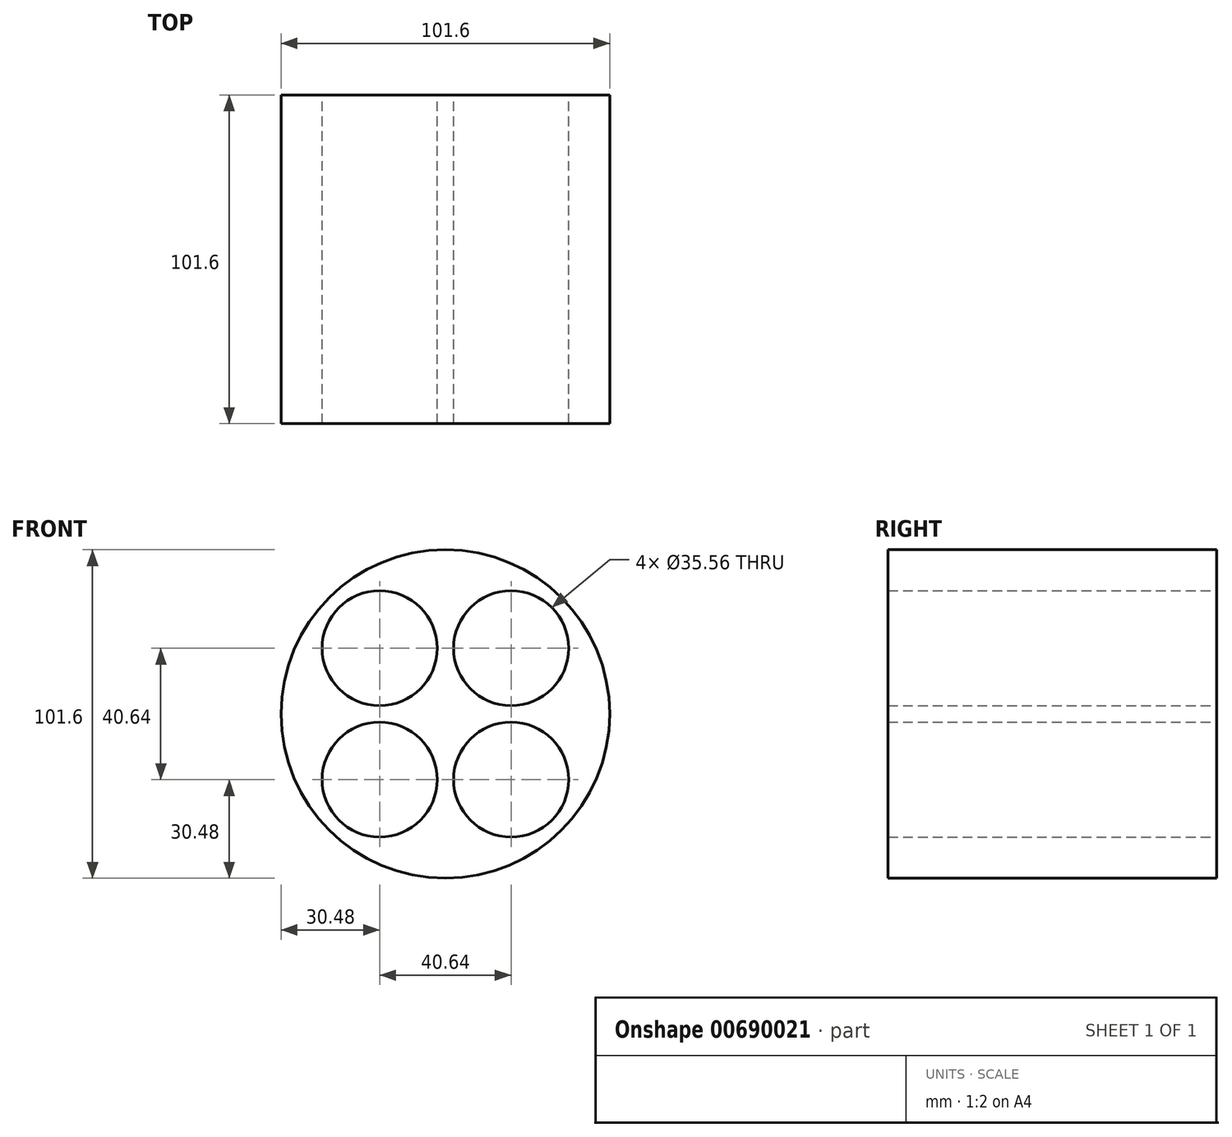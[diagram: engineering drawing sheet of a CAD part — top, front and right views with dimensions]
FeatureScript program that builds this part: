
annotation { "Feature Type Name" : "Feature", "Feature Type Description" : "" }
export const myFeature = defineFeature(function(context is Context, id is Id, definition is map)
    precondition{}
    {
        {
            var Q0;
            Q0=qCreatedBy(makeId("Front.planeOp"),FACE);
            var sketch = newSketch(context, id + "F0", { "sketchPlane" : qUnion([Q0])});
            skCircle(sketch, "E0", {"center": v(0, 0) * mm, "radius": 50.8 * mm});
            skLineSegment(sketch, "E1.bottom", {"start": v(20.32, 20.32) * mm, "end": v(-20.32, 20.32) * mm, "construction": true});
            skLineSegment(sketch, "E1.top", {"start": v(20.32, -20.32) * mm, "end": v(-20.32, -20.32) * mm, "construction": true});
            skLineSegment(sketch, "E1.left", {"start": v(20.32, 20.32) * mm, "end": v(20.32, -20.32) * mm, "construction": true});
            skLineSegment(sketch, "E1.right", {"start": v(-20.32, 20.32) * mm, "end": v(-20.32, -20.32) * mm, "construction": true});
            skCircle(sketch, "E2", {"center": v(20.32, -20.32) * mm, "radius": 17.78 * mm});
            skCircle(sketch, "E3", {"center": v(20.32, 20.32) * mm, "radius": 17.78 * mm});
            skCircle(sketch, "E4", {"center": v(-20.32, -20.32) * mm, "radius": 17.78 * mm});
            skCircle(sketch, "E5", {"center": v(-20.32, 20.32) * mm, "radius": 17.78 * mm});
            skSolve(sketch);
        }
        {
            var Q0;
            Q0=makeQuery(id+"F0.imprint","IMPRINT",FACE,{"disambiguationData":[TD([[makeQuery(id+"F0.imprint","IMPRINT",EDGE,{"derivedFrom":sQuery(id+"F0.wireOp",EDGE,"E0")}),1.0]])]});
            extrude(context, id + "F1", {"entities" : qUnion([Q0]), "depth" : 101.6 * mm, "offsetDistance" : 25.4 * mm});
        }
    });
